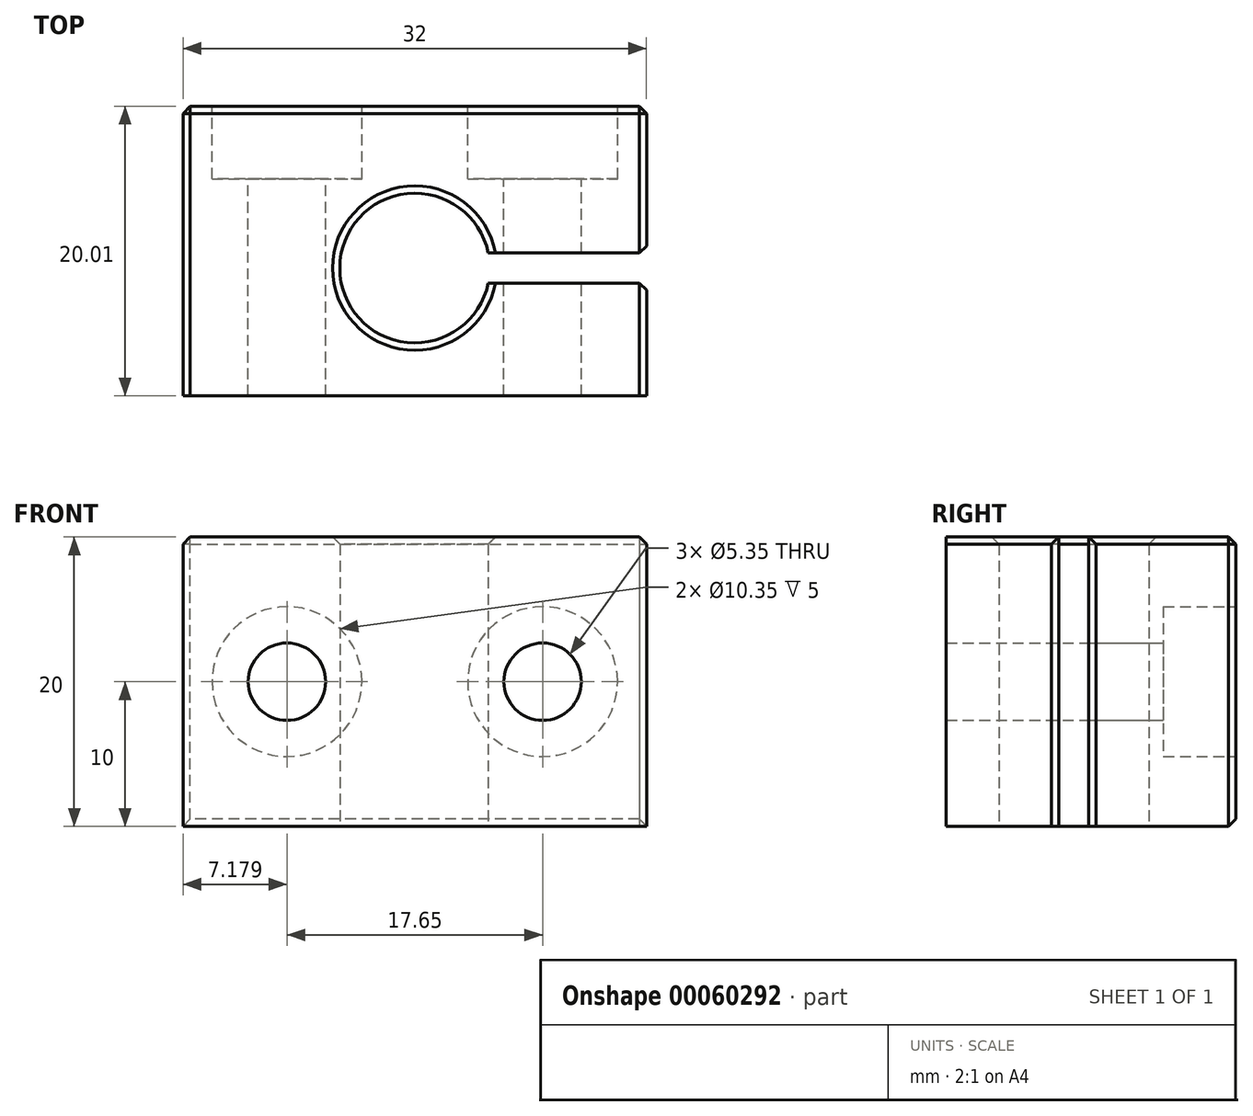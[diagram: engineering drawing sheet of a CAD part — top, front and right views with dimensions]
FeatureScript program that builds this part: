
annotation { "Feature Type Name" : "Feature", "Feature Type Description" : "" }
export const myFeature = defineFeature(function(context is Context, id is Id, definition is map)
    precondition{}
    {
        {
            var Q0;
            Q0=qCreatedBy(makeId("Top.planeOp"),FACE);
            var sketch = newSketch(context, id + "F0", { "sketchPlane" : qUnion([Q0])});
            skLineSegment(sketch, "E0.bottom", {"start": v(-17.08, 11.18) * mm, "end": v(14.92, 11.18) * mm});
            skLineSegment(sketch, "E0.left", {"start": v(-17.08, 11.18) * mm, "end": v(-17.08, -8.82) * mm});
            skLineSegment(sketch, "E0.right", {"start": v(14.92, 11.18) * mm, "end": v(14.92, 1.04) * mm});
            skArc(sketch, "E1", {"start": v(4, 1.04) * mm, "mid": v(-6.25, 0) * mm, "end": v(4, -1.04) * mm});
            skPoint(sketch, "E1.centerSnap0", {"position": v(-1.08, -9) * mm});
            skLineSegment(sketch, "E2", {"start": v(14.92, -1.04) * mm, "end": v(4, -1.04) * mm});
            skLineSegment(sketch, "E3", {"start": v(4, 1.04) * mm, "end": v(14.92, 1.04) * mm});
            skLineSegment(sketch, "E4.trimOffspring", {"start": v(14.92, -1.04) * mm, "end": v(14.92, -8.82) * mm});
            skPoint(sketch, "E5.start.orphan", {"position": v(-17.08, -18.83) * mm});
            skPoint(sketch, "E6.trimOffspring.end.orphan", {"position": v(14.92, -18.82) * mm});
            skLineSegment(sketch, "E7", {"start": v(14.92, -8.82) * mm, "end": v(-17.08, -8.82) * mm});
            skPoint(sketch, "E8.end.orphan", {"position": v(14.92, -28.82) * mm});
            skPoint(sketch, "E9.end.orphan", {"position": v(24.92, -28.82) * mm});
            skPoint(sketch, "E10.end.orphan", {"position": v(-17.08, -28.83) * mm});
            skPoint(sketch, "E11.end.orphan", {"position": v(-27.08, -28.83) * mm});
            skPoint(sketch, "E12.start.orphan", {"position": v(24.92, -1.04) * mm});
            skPoint(sketch, "E13.end.orphan", {"position": v(-27.08, -1.04) * mm});
            skSolve(sketch);
        }
        {
            var Q0;
            Q0=qSketchRegion(id+"F0",true);
            extrude(context, id + "F1", {"entities" : qUnion([Q0]), "depth" : 20 * mm});
        }
        {
            var Q0;
            Q0=makeQuery(id+"F1.opExtrude","SWEPT_FACE",FACE,{"disambiguationData":[OSD([sQuery(id+"F0.wireOp",EDGE,"E0.bottom")])]});
            var sketch = newSketch(context, id + "F2", { "sketchPlane" : qUnion([Q0])});
            skCircle(sketch, "E14", {"center": v(-7.75, 10) * mm, "radius": 5.17 * mm});
            skPoint(sketch, "E14.centerSnap0", {"position": v(-14.92, 10) * mm});
            skCircle(sketch, "E15", {"center": v(-7.75, 10) * mm, "radius": 2.67 * mm});
            skCircle(sketch, "E16", {"center": v(9.9, 10) * mm, "radius": 5.17 * mm});
            skCircle(sketch, "E17", {"center": v(9.9, 10) * mm, "radius": 2.67 * mm});
            skSolve(sketch);
        }
        {
            var Q0;
            Q0=makeQuery(id+"F2.imprint","IMPRINT",FACE,{"disambiguationData":[TD([[makeQuery(id+"F2.imprint","IMPRINT",EDGE,{"derivedFrom":sQuery(id+"F2.wireOp",EDGE,"E15")}),1.0]])]});
            var Q1;
            Q1=makeQuery(id+"F2.imprint","IMPRINT",FACE,{"disambiguationData":[TD([[makeQuery(id+"F2.imprint","IMPRINT",EDGE,{"derivedFrom":sQuery(id+"F2.wireOp",EDGE,"E17")}),1.0]])]});
            extrude(context, id + "F3", {"entities" : qUnion([Q0, Q1]), "operationType" : NewBodyOperationType.REMOVE, "oppositeDirection" : true, "depth" : 20 * mm});
        }
        {
            var Q0;
            Q0=makeQuery(id+"F2.imprint","IMPRINT",FACE,{"disambiguationData":[TD([[makeQuery(id+"F2.imprint","IMPRINT",EDGE,{"derivedFrom":sQuery(id+"F2.wireOp",EDGE,"E14")}),1.0]])]});
            var Q1;
            Q1=makeQuery(id+"F2.imprint","IMPRINT",FACE,{"disambiguationData":[TD([[makeQuery(id+"F2.imprint","IMPRINT",EDGE,{"derivedFrom":sQuery(id+"F2.wireOp",EDGE,"E16")}),1.0]])]});
            extrude(context, id + "F4", {"entities" : qUnion([Q0, Q1]), "operationType" : NewBodyOperationType.REMOVE, "oppositeDirection" : true, "depth" : 5 * mm});
        }
        {
            var Q0;
            Q0=makeQuery(id+"F1.opExtrude","SWEPT_EDGE",EDGE,{"disambiguationData":[OSD([sQuery(id+"F0.wireOp",EDGE,"E2"),sQuery(id+"F0.wireOp",EDGE,"E4.trimOffspring")])]});
            var Q1;
            Q1=makeQuery(id+"F1.opExtrude","CAP_EDGE",EDGE,{"disambiguationData":[OSD([sQuery(id+"F0.wireOp",EDGE,"E0.left")])],"isStart":false});
            var Q2;
            Q2=makeQuery(id+"F1.opExtrude","CAP_EDGE",EDGE,{"disambiguationData":[OSD([sQuery(id+"F0.wireOp",EDGE,"E0.bottom")])],"isStart":false});
            var Q3;
            Q3=makeQuery(id+"F1.opExtrude","SWEPT_EDGE",EDGE,{"disambiguationData":[OSD([sQuery(id+"F0.wireOp",EDGE,"E0.bottom"),sQuery(id+"F0.wireOp",EDGE,"E0.left")])]});
            var Q4;
            Q4=makeQuery(id+"F1.opExtrude","SWEPT_EDGE",EDGE,{"disambiguationData":[OSD([sQuery(id+"F0.wireOp",EDGE,"E0.bottom"),sQuery(id+"F0.wireOp",EDGE,"E0.right")])]});
            var Q5;
            Q5=makeQuery(id+"F1.opExtrude","CAP_EDGE",EDGE,{"disambiguationData":[OSD([sQuery(id+"F0.wireOp",EDGE,"E0.right")])],"isStart":false});
            var Q6;
            Q6=makeQuery(id+"F1.opExtrude","CAP_EDGE",EDGE,{"disambiguationData":[OSD([sQuery(id+"F0.wireOp",EDGE,"E4.trimOffspring")])],"isStart":false});
            var Q7;
            Q7=makeQuery(id+"F1.opExtrude","CAP_EDGE",EDGE,{"disambiguationData":[OSD([sQuery(id+"F0.wireOp",EDGE,"E1")])],"isStart":false});
            var Q8;
            Q8=makeQuery(id+"F1.opExtrude","SWEPT_EDGE",EDGE,{"disambiguationData":[OSD([sQuery(id+"F0.wireOp",EDGE,"E0.bottom"),sQuery(id+"F0.wireOp",EDGE,"E0.left")])]});
            var Q9;
            Q9=makeQuery(id+"F1.opExtrude","SWEPT_EDGE",EDGE,{"disambiguationData":[OSD([sQuery(id+"F0.wireOp",EDGE,"E0.right"),sQuery(id+"F0.wireOp",EDGE,"E3")])]});
            var Q10;
            Q10=makeQuery(id+"F1.opExtrude","CAP_EDGE",EDGE,{"disambiguationData":[OSD([sQuery(id+"F0.wireOp",EDGE,"E0.bottom")])],"isStart":true});
            chamfer(context, id + "F5", {"entities" : qUnion([Q0, Q1, Q2, Q3, Q4, Q5, Q6, Q7, Q8, Q9, Q10]), "width" : 0.5 * mm, "tangentPropagation" : true});
        }
    });
